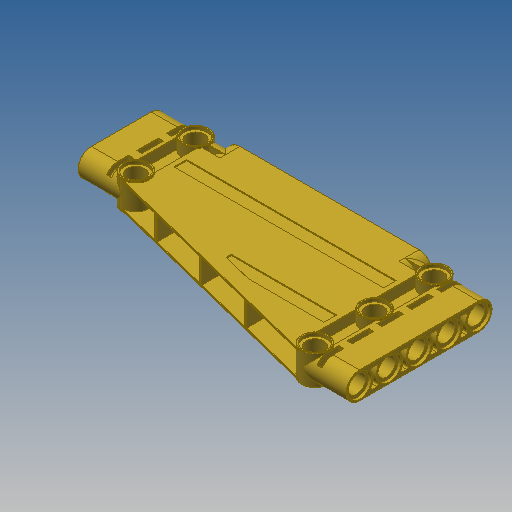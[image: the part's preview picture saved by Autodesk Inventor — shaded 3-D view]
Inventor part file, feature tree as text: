
AUTODESK INVENTOR PART (.ipt)
format: ipt  version: 2022.2 (Build 262287010, 287A)  size: 1,189,888 bytes
history: native  units: in
note: dims shown in document units (in); Inventor stores cm internally (conversion verified against a paired STEP export)
features: extrude x26, sketch x6, projected_geometry x2, plane x1, mirror x1, fillet x1
ambient origin geometry x8: Origin, YZ Plane, XZ Plane, XY Plane, X Axis, Y Axis, Z Axis, Center Point
bodies: Solid3 (feature_tree)
feature tree (37):
  sketch  "Sketch3"  dims[d15=0.189in d16=2.5197in]
  extrude  "Extrusion3"  Depth=0.252in
  plane  "Work Plane1"
  sketch  "Sketch2"  dims[d13=0.2835in d14=0.252in]
  extrude  "Extrusion6"  Depth=2.5197in
  extrude  "Extrusion8"  TaperAngle=45.0deg  [1 undecoded]
  extrude  "Extrusion9"  TaperAngle=0.0deg  [1 undecoded]
  extrude  "Extrusion10"  TaperAngle=0.0deg  [1 undecoded]
  extrude  "Extrusion11"  TaperAngle=0.0deg  [1 undecoded]
  extrude  "Extrusion7"  Depth=0.3937in TaperAngle=0.0deg
  extrude  "Extrusion12"  Depth=0.0157in TaperAngle=0.0deg
  extrude  "Extrusion4"  Depth=0.0157in
  sketch  "Sketch5"  dims[d19=0.2835in d20=0.0in]
  extrude  "Extrusion13"  TaperAngle=0.0deg  [1 undecoded]
  extrude  "Extrusion14"  Depth=0.0157in
  extrude  "Extrusion15"  TaperAngle=0.0deg  [1 undecoded]
  extrude  "Extrusion16"  Depth=0.2205in TaperAngle=0.0deg
  extrude  "Extrusion17"  Depth=0.2205in TaperAngle=0.0deg
  extrude  "Extrusion18"  Depth=0.2205in TaperAngle=0.0deg
  sketch  "Sketch6"  dims[d21=0.063in d22=0.0in]
  extrude  "Extrusion21"  Depth=0.0157in
  extrude  "Extrusion22"  Depth=0.2205in TaperAngle=0.0deg
  extrude  "Extrusion23"  Depth=0.0157in
  extrude  "Extrusion24"  Depth=0.0157in
  extrude  "Extrusion25"  TaperAngle=45.0deg  [1 undecoded]
  extrude  "Extrusion26"  Depth=0.0157in TaperAngle=0.0deg
  extrude  "Extrusion5"  Depth=0.0157in TaperAngle=0.0deg
  extrude  "Extrusion19"  Depth=0.0157in TaperAngle=0.0deg
  extrude  "Extrusion20"  Depth=0.0157in TaperAngle=0.0deg
  sketch  "Sketch7"  dims[d23=0.315in d24=0.0in d37=0.3937in d38=0.0in d39=0.2117in d40=0.0in d41=0.2835in d42=0.0in d43=0.0315in d44=0.0in d45=0.2205in d46=0.0in d47=0.2205in d48=0.0in d49=0.2205in d50=0.0in d51=0.2835in d52=0.2205in d53=0.0in d54=0.252in d55=0.189in d56=45.0deg d57=0.3723in d58=0.0in d59=0.0416in d60=0.0in d61=0.3408in d62=0.0in d63=0.1518in d64=0.0in d65=0.1518in d66=0.0in d67=0.1518in d68=0.0in d69=0.252in d70=0.0in d71=0.2835in d72=0.252in d73=0.189in d74=45.0deg d75=0.252in d76=0.0in d77=0.252in d78=0.0in d79=0.3723in d80=0.0in d81=0.0416in d82=0.0in d83=0.3408in d84=0.0in d85=0.1518in d86=0.0in d87=-0.7874in d88=0.315in d89=0.189in d90=0.2441in d93=0.0315in d94=0.0315in d95=0.0315in d100=45.0deg d101=0.0416in d102=0.0416in d103=0.0472in d104=0.2205in d105=2.2047in d106=0.4094in d107=0.126in d108=0.5039in d109=1.1024in d110=0.0487in d111=0.0079in d112=0.0in d113=0.0079in d114=0.0in d115=0.0039in d116=0.0157in]
  extrude  "Extrusion27"  Depth=0.0157in TaperAngle=0.0deg
  mirror  "Mirror1"
  extrude  "Extrusion28"  Depth=0.0157in TaperAngle=0.0deg
  fillet  "Fillet1"  Radius=0.252in
  sketch  "Sketch4"  dims[d17=0.6299in d18=45.0deg]
  projected_geometry  "Projected Loop1"
  projected_geometry  "Projected Loop2"
note: 7 required parameter values undecoded (feature->parameter linkage not recoverable at this tier; creation-order binding heuristic only, values carry confidence <= 0.55)
